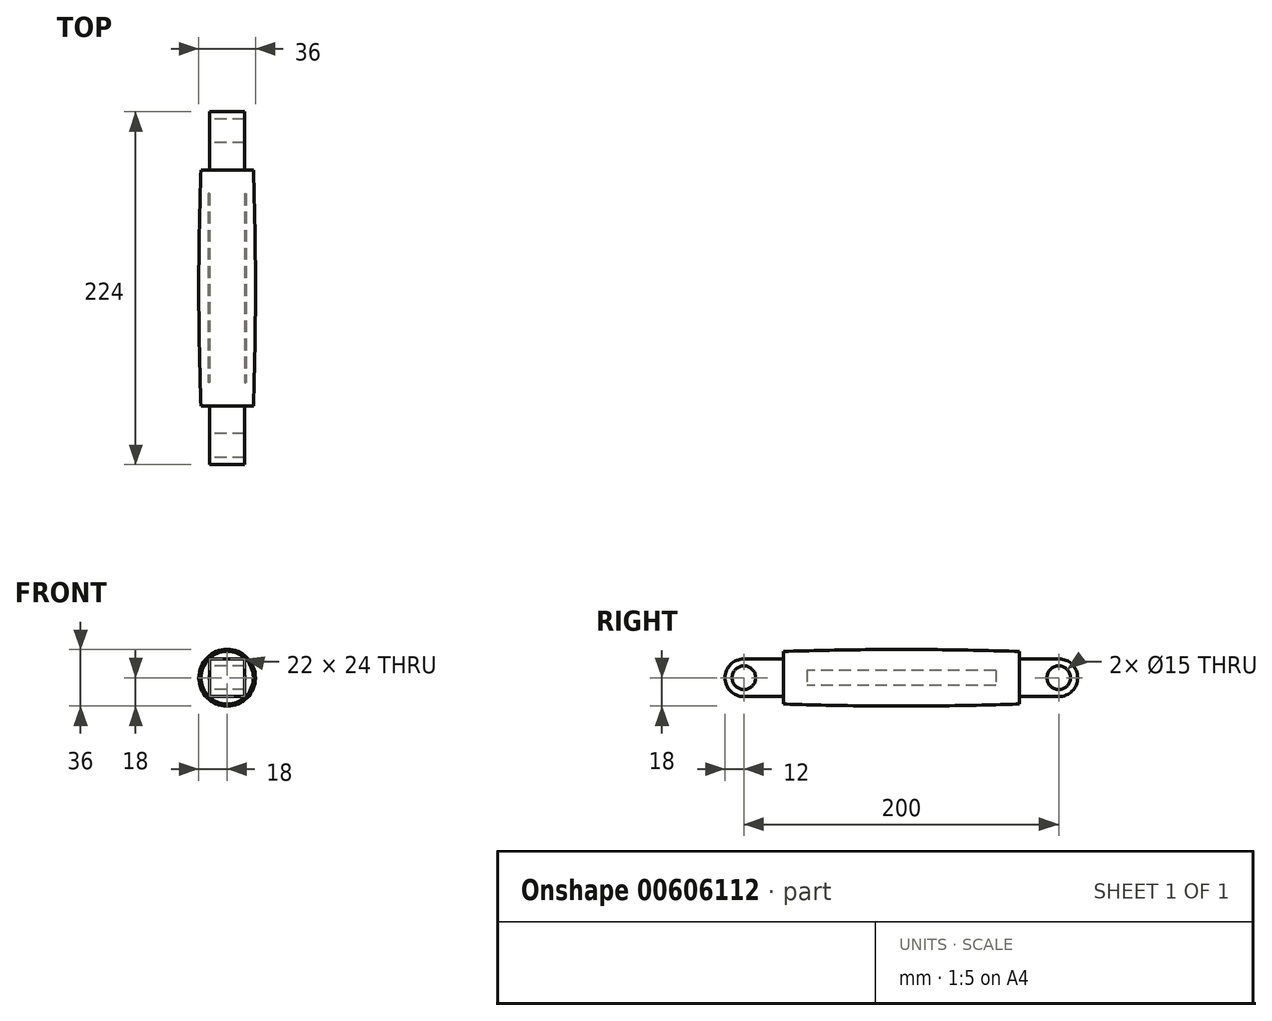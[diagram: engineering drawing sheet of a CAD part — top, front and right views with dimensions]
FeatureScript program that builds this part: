
annotation { "Feature Type Name" : "Feature", "Feature Type Description" : "" }
export const myFeature = defineFeature(function(context is Context, id is Id, definition is map)
    precondition{}
    {
        {
            var Q0;
            Q0=qCreatedBy(makeId("Right.planeOp"),FACE);
            var sketch = newSketch(context, id + "F0", { "sketchPlane" : qUnion([Q0])});
            skLineSegment(sketch, "E0.bottom", {"start": v(100, 12) * mm, "end": v(-100, 12) * mm});
            skLineSegment(sketch, "E0.top", {"start": v(100, -12) * mm, "end": v(-100, -12) * mm});
            skLineSegment(sketch, "E0.left", {"start": v(100, 12) * mm, "end": v(100, -12) * mm});
            skLineSegment(sketch, "E0.right", {"start": v(-100, 12) * mm, "end": v(-100, -12) * mm});
            skPoint(sketch, "E0.middle", {"position": v(0, 0) * mm});
            skCircle(sketch, "E1", {"center": v(100, 0) * mm, "radius": 12 * mm});
            skCircle(sketch, "E2", {"center": v(100, 0) * mm, "radius": 7.5 * mm});
            skCircle(sketch, "E3", {"center": v(-100, 0) * mm, "radius": 7.5 * mm});
            skCircle(sketch, "E4", {"center": v(-100, 0) * mm, "radius": 12 * mm});
            skSolve(sketch);
        }
        {
            var Q0;
            {var subQ0=sQuery(id+"F0.wireOp",EDGE,"E0.bottom");Q0=makeQuery(id+"F0.imprint","IMPRINT",FACE,{"disambiguationData":[TD([[makeQuery(id+"F0.imprint","IMPRINT",EDGE,{"derivedFrom":subQ0}),1.0]])]});}
            var Q1;
            {var subQ1=sQuery(id+"F0.wireOp",EDGE,"E0.right");var subQ3=sQuery(id+"F0.wireOp",EDGE,"E3");var subQ4=makeQuery(id+"F0.imprint","INTERSECT",VERTEX,{"disambiguationData":[OD(0.0)],"derivedFrom":[subQ1,subQ3]});Q1=makeQuery(id+"F0.imprint","IMPRINT",FACE,{"disambiguationData":[TD([[makeQuery(id+"F0.imprint","IMPRINT",EDGE,{"disambiguationData":[TD([[subQ4,-1.0]])],"derivedFrom":subQ3}),-1.0]])]});}
            var Q2;
            {var subQ1=sQuery(id+"F0.wireOp",EDGE,"E0.right");var subQ3=sQuery(id+"F0.wireOp",EDGE,"E3");var subQ4=makeQuery(id+"F0.imprint","INTERSECT",VERTEX,{"disambiguationData":[OD(0.0)],"derivedFrom":[subQ1,subQ3]});Q2=makeQuery(id+"F0.imprint","IMPRINT",FACE,{"disambiguationData":[TD([[makeQuery(id+"F0.imprint","IMPRINT",EDGE,{"disambiguationData":[TD([[subQ4,1.0]])],"derivedFrom":subQ3}),-1.0]])]});}
            var Q3;
            {var subQ1=sQuery(id+"F0.wireOp",EDGE,"E0.left");var subQ3=sQuery(id+"F0.wireOp",EDGE,"E2");var subQ4=makeQuery(id+"F0.imprint","INTERSECT",VERTEX,{"disambiguationData":[OD(0.0)],"derivedFrom":[subQ1,subQ3]});Q3=makeQuery(id+"F0.imprint","IMPRINT",FACE,{"disambiguationData":[TD([[makeQuery(id+"F0.imprint","IMPRINT",EDGE,{"disambiguationData":[TD([[subQ4,-1.0]])],"derivedFrom":subQ3}),-1.0]])]});}
            var Q4;
            {var subQ1=sQuery(id+"F0.wireOp",EDGE,"E0.left");var subQ3=sQuery(id+"F0.wireOp",EDGE,"E2");var subQ4=makeQuery(id+"F0.imprint","INTERSECT",VERTEX,{"disambiguationData":[OD(0.0)],"derivedFrom":[subQ1,subQ3]});Q4=makeQuery(id+"F0.imprint","IMPRINT",FACE,{"disambiguationData":[TD([[makeQuery(id+"F0.imprint","IMPRINT",EDGE,{"disambiguationData":[TD([[subQ4,1.0]])],"derivedFrom":subQ3}),-1.0]])]});}
            extrude(context, id + "F1", {"entities" : qUnion([Q0, Q1, Q2, Q3, Q4]), "endBound" : BoundingType.SYMMETRIC, "depth" : 22 * mm, "offsetDistance" : 25.4 * mm});
        }
        {
            var Q0;
            Q0=qCreatedBy(makeId("Right.planeOp"),FACE);
            var sketch = newSketch(context, id + "F2", { "sketchPlane" : qUnion([Q0])});
            skLineSegment(sketch, "E5.bottom", {"start": v(-60, -12) * mm, "end": v(60, -12) * mm});
            skLineSegment(sketch, "E5.top", {"start": v(-60, 12) * mm, "end": v(60, 12) * mm});
            skLineSegment(sketch, "E5.left", {"start": v(-60, -12) * mm, "end": v(-60, 12) * mm});
            skLineSegment(sketch, "E5.right", {"start": v(60, -12) * mm, "end": v(60, 12) * mm});
            skPoint(sketch, "E5.middle", {"position": v(0, 0) * mm});
            skLineSegment(sketch, "E6.bottom", {"start": v(80, 16.5) * mm, "end": v(-80, 16.5) * mm});
            skLineSegment(sketch, "E6.top", {"start": v(80, -16.5) * mm, "end": v(-80, -16.5) * mm});
            skLineSegment(sketch, "E6.left", {"start": v(80, 16.5) * mm, "end": v(80, -16.5) * mm});
            skLineSegment(sketch, "E6.right", {"start": v(-80, 16.5) * mm, "end": v(-80, -16.5) * mm});
            skLineSegment(sketch, "E7.bottom", {"start": v(75, 18) * mm, "end": v(-75, 18) * mm});
            skLineSegment(sketch, "E7.top", {"start": v(75, -18) * mm, "end": v(-75, -18) * mm});
            skLineSegment(sketch, "E7.left", {"start": v(75, 18) * mm, "end": v(75, -18) * mm});
            skLineSegment(sketch, "E7.right", {"start": v(-75, 18) * mm, "end": v(-75, -18) * mm});
            skFitSpline(sketch, "E8", {"points": [v(-80, 16.5) * mm, v(0, 18) * mm, v(80, 16.5) * mm], "startDerivative": vector(80, 3) * mm, "endDerivative": vector(80, -3) * mm});
            skLineSegment(sketch, "E9", {"start": v(-80, 0) * mm, "end": v(80, 0) * mm});
            skSolve(sketch);
        }
        {
            var Q0;
            {var subQ4=sQuery(id+"F2.wireOp",EDGE,"E6.bottom");var subQ6=sQuery(id+"F2.wireOp",EDGE,"E7.left");var subQ8=makeQuery(id+"F2.imprint","INTERSECT",VERTEX,{"derivedFrom":[subQ4,subQ6]});Q0=makeQuery(id+"F2.imprint","IMPRINT",FACE,{"disambiguationData":[TD([[makeQuery(id+"F2.imprint","IMPRINT",EDGE,{"disambiguationData":[TD([[subQ8,-1.0]])],"derivedFrom":subQ4}),-1.0]])]});}
            var Q1;
            {var subQ0=sQuery(id+"F2.wireOp",EDGE,"E7.right");var subQ1=sQuery(id+"F2.wireOp",EDGE,"E5.top");var subQ2=makeQuery(id+"F2.imprint","INTERSECT",VERTEX,{"derivedFrom":[subQ1,subQ0]});Q1=makeQuery(id+"F2.imprint","IMPRINT",FACE,{"disambiguationData":[TD([[makeQuery(id+"F2.imprint","IMPRINT",EDGE,{"disambiguationData":[TD([[subQ2,-1.0]])],"derivedFrom":subQ1}),1.0]])]});}
            var Q2;
            Q2=sQuery(id+"F2.wireOp",EDGE,"E9");
            revolve(context, id + "F3", {"operationType" : NewBodyOperationType.ADD, "entities" : qUnion([Q0, Q1]), "axis" : qUnion([Q2]), "revolveType" : RevolveType.FULL});
        }
    });
